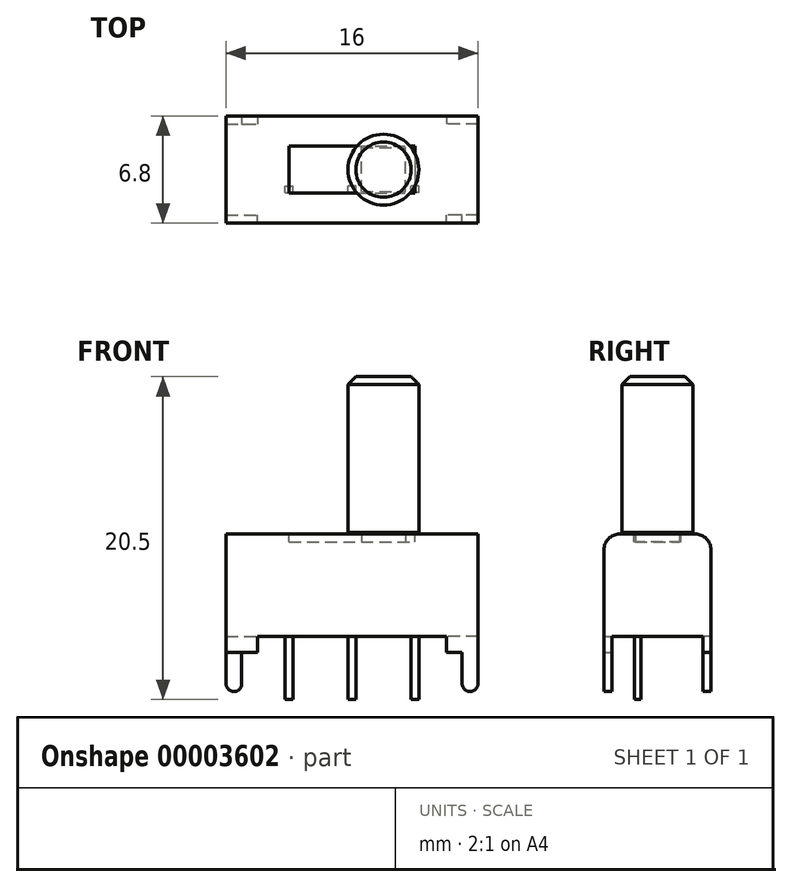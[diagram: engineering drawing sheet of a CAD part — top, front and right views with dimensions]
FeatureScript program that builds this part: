
annotation { "Feature Type Name" : "Feature", "Feature Type Description" : "" }
export const myFeature = defineFeature(function(context is Context, id is Id, definition is map)
    precondition{}
    {
        {
            var Q0;
            Q0=qCreatedBy(makeId("Front.planeOp"),FACE);
            var sketch = newSketch(context, id + "F0", { "sketchPlane" : qUnion([Q0])});
            skLineSegment(sketch, "E0.bottom", {"start": v(0, 0) * mm, "end": v(-16, 0) * mm});
            skLineSegment(sketch, "E0.top", {"start": v(0, 6.5) * mm, "end": v(-16, 6.5) * mm});
            skLineSegment(sketch, "E0.left", {"start": v(0, 0) * mm, "end": v(0, 6.5) * mm});
            skLineSegment(sketch, "E0.right", {"start": v(-16, 0) * mm, "end": v(-16, 6.5) * mm});
            skSolve(sketch);
        }
        {
            var Q0;
            Q0 = qSketchRegion(id + "F0", true);
            extrude(context, id + "F1", {"entities" : qUnion([Q0]), "depth" : 6.8 * mm});
        }
        {
            var Q0;
            Q0=makeQuery(id+"F1.opExtrude","SWEPT_FACE",FACE,{"disambiguationData":[OSD([sQuery(id+"F0.wireOp",EDGE,"E0.bottom")])]});
            var sketch = newSketch(context, id + "F2", { "sketchPlane" : qUnion([Q0])});
            skLineSegment(sketch, "E1.bottom", {"start": v(0, 0) * mm, "end": v(-2, 0) * mm});
            skLineSegment(sketch, "E1.top", {"start": v(0, 0.5) * mm, "end": v(-2, 0.5) * mm});
            skLineSegment(sketch, "E1.left", {"start": v(0, 0) * mm, "end": v(0, 0.5) * mm});
            skLineSegment(sketch, "E1.right", {"start": v(-2, 0) * mm, "end": v(-2, 0.5) * mm});
            skLineSegment(sketch, "E2", {"start": v(-8, 0) * mm, "end": v(-8, 6.8) * mm, "construction": true});
            skLineSegment(sketch, "E3", {"start": v(0, 3.4) * mm, "end": v(-16, 3.4) * mm, "construction": true});
            skLineSegment(sketch, "E4.0.MirrorCS", {"start": v(0, 6.8) * mm, "end": v(0, 6.3) * mm});
            skLineSegment(sketch, "E4.1.MirrorCS", {"start": v(0, 6.3) * mm, "end": v(-2, 6.3) * mm});
            skLineSegment(sketch, "E4.2.MirrorCS", {"start": v(-2, 6.8) * mm, "end": v(-2, 6.3) * mm});
            skLineSegment(sketch, "E4.3.MirrorCS", {"start": v(0, 6.8) * mm, "end": v(-2, 6.8) * mm});
            skLineSegment(sketch, "E5.0.MirrorCS", {"start": v(-16, 6.3) * mm, "end": v(-14, 6.3) * mm});
            skLineSegment(sketch, "E5.1.MirrorCS", {"start": v(-14, 6.8) * mm, "end": v(-14, 6.3) * mm});
            skLineSegment(sketch, "E5.2.MirrorCS", {"start": v(-16, 6.8) * mm, "end": v(-14, 6.8) * mm});
            skLineSegment(sketch, "E5.3.MirrorCS", {"start": v(-16, 6.8) * mm, "end": v(-16, 6.3) * mm});
            skLineSegment(sketch, "E5.4.MirrorCS", {"start": v(-16, 0) * mm, "end": v(-16, 0.5) * mm});
            skLineSegment(sketch, "E5.5.MirrorCS", {"start": v(-16, 0.5) * mm, "end": v(-14, 0.5) * mm});
            skLineSegment(sketch, "E5.6.MirrorCS", {"start": v(-16, 0) * mm, "end": v(-14, 0) * mm});
            skLineSegment(sketch, "E5.7.MirrorCS", {"start": v(-14, 0) * mm, "end": v(-14, 0.5) * mm});
            skSolve(sketch);
        }
        {
            var Q0;
            Q0 = qSketchRegion(id + "F2", true);
            extrude(context, id + "F3", {"entities" : qUnion([Q0]), "operationType" : NewBodyOperationType.ADD, "depth" : 1 * mm});
        }
        {
            var Q0;
            Q0=makeQuery(id+"F3.opExtrude","CAP_FACE",FACE,{"disambiguationData":[OSD([sQuery(id+"F2.wireOp",EDGE,"E1.bottom"),sQuery(id+"F2.wireOp",EDGE,"E1.top"),sQuery(id+"F2.wireOp",EDGE,"E1.left"),sQuery(id+"F2.wireOp",EDGE,"E1.right")])],"isStart":false});
            var sketch = newSketch(context, id + "F4", { "sketchPlane" : qUnion([Q0])});
            skLineSegment(sketch, "E6.bottom", {"start": v(-16, 0) * mm, "end": v(-15, 0) * mm});
            skLineSegment(sketch, "E6.top", {"start": v(-16, 0.5) * mm, "end": v(-15, 0.5) * mm});
            skLineSegment(sketch, "E6.left", {"start": v(-16, 0) * mm, "end": v(-16, 0.5) * mm});
            skLineSegment(sketch, "E6.right", {"start": v(-15, 0) * mm, "end": v(-15, 0.5) * mm});
            skLineSegment(sketch, "E7.bottom", {"start": v(0, 6.8) * mm, "end": v(-1, 6.8) * mm});
            skLineSegment(sketch, "E7.top", {"start": v(0, 6.3) * mm, "end": v(-1, 6.3) * mm});
            skLineSegment(sketch, "E7.left", {"start": v(0, 6.8) * mm, "end": v(0, 6.3) * mm});
            skLineSegment(sketch, "E7.right", {"start": v(-1, 6.8) * mm, "end": v(-1, 6.3) * mm});
            skSolve(sketch);
        }
        {
            var Q0;
            Q0 = qSketchRegion(id + "F4", true);
            extrude(context, id + "F5", {"entities" : qUnion([Q0]), "operationType" : NewBodyOperationType.ADD, "depth" : 2.5 * mm});
        }
        {
            var Q0;
            Q0=makeQuery(id+"F1.opExtrude","SWEPT_FACE",FACE,{"disambiguationData":[OSD([sQuery(id+"F0.wireOp",EDGE,"E0.top")])]});
            var sketch = newSketch(context, id + "F6", { "sketchPlane" : qUnion([Q0])});
            skLineSegment(sketch, "E8.bottom", {"start": v(-12, -1.9) * mm, "end": v(-4, -1.9) * mm});
            skLineSegment(sketch, "E8.top", {"start": v(-12, -4.9) * mm, "end": v(-4, -4.9) * mm});
            skLineSegment(sketch, "E8.left", {"start": v(-12, -1.9) * mm, "end": v(-12, -4.9) * mm});
            skLineSegment(sketch, "E8.right", {"start": v(-4, -1.9) * mm, "end": v(-4, -4.9) * mm});
            skLineSegment(sketch, "E9", {"start": v(-4, -3.4) * mm, "end": v(0, -3.4) * mm, "construction": true});
            skLineSegment(sketch, "E10", {"start": v(-12, -3.4) * mm, "end": v(-16, -3.4) * mm, "construction": true});
            skLineSegment(sketch, "E11", {"start": v(-8, -4.9) * mm, "end": v(-8, -6.8) * mm, "construction": true});
            skLineSegment(sketch, "E12", {"start": v(-8, -1.9) * mm, "end": v(-8, 0) * mm, "construction": true});
            skSolve(sketch);
        }
        {
            var Q0;
            Q0 = qSketchRegion(id + "F6", true);
            extrude(context, id + "F7", {"entities" : qUnion([Q0]), "operationType" : NewBodyOperationType.REMOVE, "oppositeDirection" : true, "depth" : 0.5 * mm});
        }
        {
            var Q0;
            Q0=makeQuery(id+"F7.boolean.opBoolean","COPY",FACE,{"derivedFrom":makeQuery(id+"F7.opExtrude","CAP_FACE",FACE,{"disambiguationData":[OSD([sQuery(id+"F6.wireOp",EDGE,"E8.bottom"),sQuery(id+"F6.wireOp",EDGE,"E8.top"),sQuery(id+"F6.wireOp",EDGE,"E8.left"),sQuery(id+"F6.wireOp",EDGE,"E8.right")])],"isStart":false})});
            var sketch = newSketch(context, id + "F8", { "sketchPlane" : qUnion([Q0])});
            skLineSegment(sketch, "E13.bottom", {"start": v(-7.4, -4.8) * mm, "end": v(-4.6, -4.8) * mm});
            skLineSegment(sketch, "E13.top", {"start": v(-7.4, -2) * mm, "end": v(-4.6, -2) * mm});
            skLineSegment(sketch, "E13.left", {"start": v(-7.4, -4.8) * mm, "end": v(-7.4, -2) * mm});
            skLineSegment(sketch, "E13.right", {"start": v(-4.6, -4.8) * mm, "end": v(-4.6, -2) * mm});
            skLineSegment(sketch, "E14", {"start": v(-4.6, -3.4) * mm, "end": v(-4, -3.4) * mm, "construction": true});
            skLineSegment(sketch, "E15", {"start": v(-4.6, -4.8) * mm, "end": v(-4.6, -4.9) * mm, "construction": true});
            skLineSegment(sketch, "E16", {"start": v(-4.6, -4.8) * mm, "end": v(-7.4, -2) * mm, "construction": true});
            skLineSegment(sketch, "E17", {"start": v(-8, -4.9) * mm, "end": v(-8, -1.9) * mm, "construction": true});
            skPoint(sketch, "E18", {"position": v(-6, -3.4) * mm});
            skSolve(sketch);
        }
        {
            var Q0;
            Q0 = qSketchRegion(id + "F8", true);
            extrude(context, id + "F9", {"entities" : qUnion([Q0]), "operationType" : NewBodyOperationType.ADD, "depth" : 0.6 * mm});
        }
        {
            var Q0;
            Q0=makeQuery(id+"F9.opExtrude","CAP_FACE",FACE,{"disambiguationData":[OSD([sQuery(id+"F8.wireOp",EDGE,"E13.bottom"),sQuery(id+"F8.wireOp",EDGE,"E13.top"),sQuery(id+"F8.wireOp",EDGE,"E13.left"),sQuery(id+"F8.wireOp",EDGE,"E13.right")])],"isStart":false});
            var sketch = newSketch(context, id + "F10", { "sketchPlane" : qUnion([Q0])});
            skLineSegment(sketch, "E19", {"start": v(-7.4, -2) * mm, "end": v(-4.6, -4.8) * mm, "construction": true});
            skCircle(sketch, "E20", {"center": v(-6, -3.4) * mm, "radius": 2.25 * mm});
            skSolve(sketch);
        }
        {
            var Q0;
            Q0 = qSketchRegion(id + "F10", true);
            extrude(context, id + "F11", {"entities" : qUnion([Q0]), "depth" : 9.9 * mm});
        }
        {
            var Q0;
            Q0=makeQuery(id+"F11.opExtrude","CAP_EDGE",EDGE,{"disambiguationData":[OSD([sQuery(id+"F10.wireOp",EDGE,"E20")])],"isStart":false});
            chamfer(context, id + "F12", {"entities" : qUnion([Q0]), "width" : 0.5 * mm, "tangentPropagation" : true});
        }
        {
            var Q0;
            Q0=makeQuery(id+"F1.opExtrude","SWEPT_FACE",FACE,{"disambiguationData":[OSD([sQuery(id+"F0.wireOp",EDGE,"E0.bottom")])]});
            var sketch = newSketch(context, id + "F13", { "sketchPlane" : qUnion([Q0])});
            skLineSegment(sketch, "E21", {"start": v(-16, 4.65) * mm, "end": v(0, 4.65) * mm, "construction": true});
            skPoint(sketch, "E22", {"position": v(0, 6.55) * mm});
            skLineSegment(sketch, "E23.rect.bottom", {"start": v(-7.75, 4.85) * mm, "end": v(-8.25, 4.85) * mm});
            skLineSegment(sketch, "E23.rect.top", {"start": v(-7.75, 4.45) * mm, "end": v(-8.25, 4.45) * mm});
            skLineSegment(sketch, "E23.rect.left", {"start": v(-7.75, 4.85) * mm, "end": v(-7.75, 4.45) * mm});
            skLineSegment(sketch, "E23.rect.right", {"start": v(-8.25, 4.85) * mm, "end": v(-8.25, 4.45) * mm});
            skPoint(sketch, "E23.rect.middle", {"position": v(-8, 4.65) * mm});
            skLineSegment(sketch, "E24.rect.bottom", {"start": v(-3.75, 4.85) * mm, "end": v(-4.25, 4.85) * mm});
            skLineSegment(sketch, "E24.rect.top", {"start": v(-3.75, 4.45) * mm, "end": v(-4.25, 4.45) * mm});
            skLineSegment(sketch, "E24.rect.left", {"start": v(-3.75, 4.85) * mm, "end": v(-3.75, 4.45) * mm});
            skLineSegment(sketch, "E24.rect.right", {"start": v(-4.25, 4.85) * mm, "end": v(-4.25, 4.45) * mm});
            skPoint(sketch, "E24.rect.middle", {"position": v(-4, 4.65) * mm});
            skLineSegment(sketch, "E25", {"start": v(-8, 4.65) * mm, "end": v(-8, 6.8) * mm, "construction": true});
            skLineSegment(sketch, "E26.0.MirrorCS", {"start": v(-12.25, 4.45) * mm, "end": v(-11.75, 4.45) * mm});
            skLineSegment(sketch, "E26.1.MirrorCS", {"start": v(-11.75, 4.85) * mm, "end": v(-11.75, 4.45) * mm});
            skLineSegment(sketch, "E26.2.MirrorCS", {"start": v(-12.25, 4.85) * mm, "end": v(-12.25, 4.45) * mm});
            skPoint(sketch, "E26.3.MirrorP", {"position": v(-12, 4.65) * mm});
            skLineSegment(sketch, "E26.4.MirrorCS", {"start": v(-12.25, 4.85) * mm, "end": v(-11.75, 4.85) * mm});
            skSolve(sketch);
        }
        {
            var Q0;
            Q0 = qSketchRegion(id + "F13", true);
            extrude(context, id + "F14", {"entities" : qUnion([Q0]), "operationType" : NewBodyOperationType.ADD, "depth" : 4 * mm});
        }
        {
            var Q0;
            Q0=makeQuery(id+"F1.opExtrude","CAP_EDGE",EDGE,{"disambiguationData":[OSD([sQuery(id+"F0.wireOp",EDGE,"E0.top")])],"isStart":false});
            var Q1;
            Q1=makeQuery(id+"F1.opExtrude","CAP_EDGE",EDGE,{"disambiguationData":[OSD([sQuery(id+"F0.wireOp",EDGE,"E0.top")])],"isStart":true});
            fillet(context, id + "F15", {"entities" : qUnion([Q0, Q1]), "radius" : 1 * mm, "allowEdgeOverflow" : false});
        }
        {
            var Q0;
            Q0=makeQuery(id+"F5.opExtrude","CAP_EDGE",EDGE,{"disambiguationData":[OSD([sQuery(id+"F4.wireOp",EDGE,"E6.left")])],"isStart":false});
            var Q1;
            Q1=makeQuery(id+"F5.opExtrude","CAP_EDGE",EDGE,{"disambiguationData":[OSD([sQuery(id+"F4.wireOp",EDGE,"E6.right")])],"isStart":false});
            var Q2;
            Q2=makeQuery(id+"F5.opExtrude","CAP_EDGE",EDGE,{"disambiguationData":[OSD([sQuery(id+"F4.wireOp",EDGE,"E7.right")])],"isStart":false});
            var Q3;
            Q3=makeQuery(id+"F5.opExtrude","CAP_EDGE",EDGE,{"disambiguationData":[OSD([sQuery(id+"F4.wireOp",EDGE,"E7.left")])],"isStart":false});
            fillet(context, id + "F16", {"entities" : qUnion([Q0, Q1, Q2, Q3]), "radius" : 0.5 * mm, "tangentPropagation" : true, "allowEdgeOverflow" : false});
        }
    });
